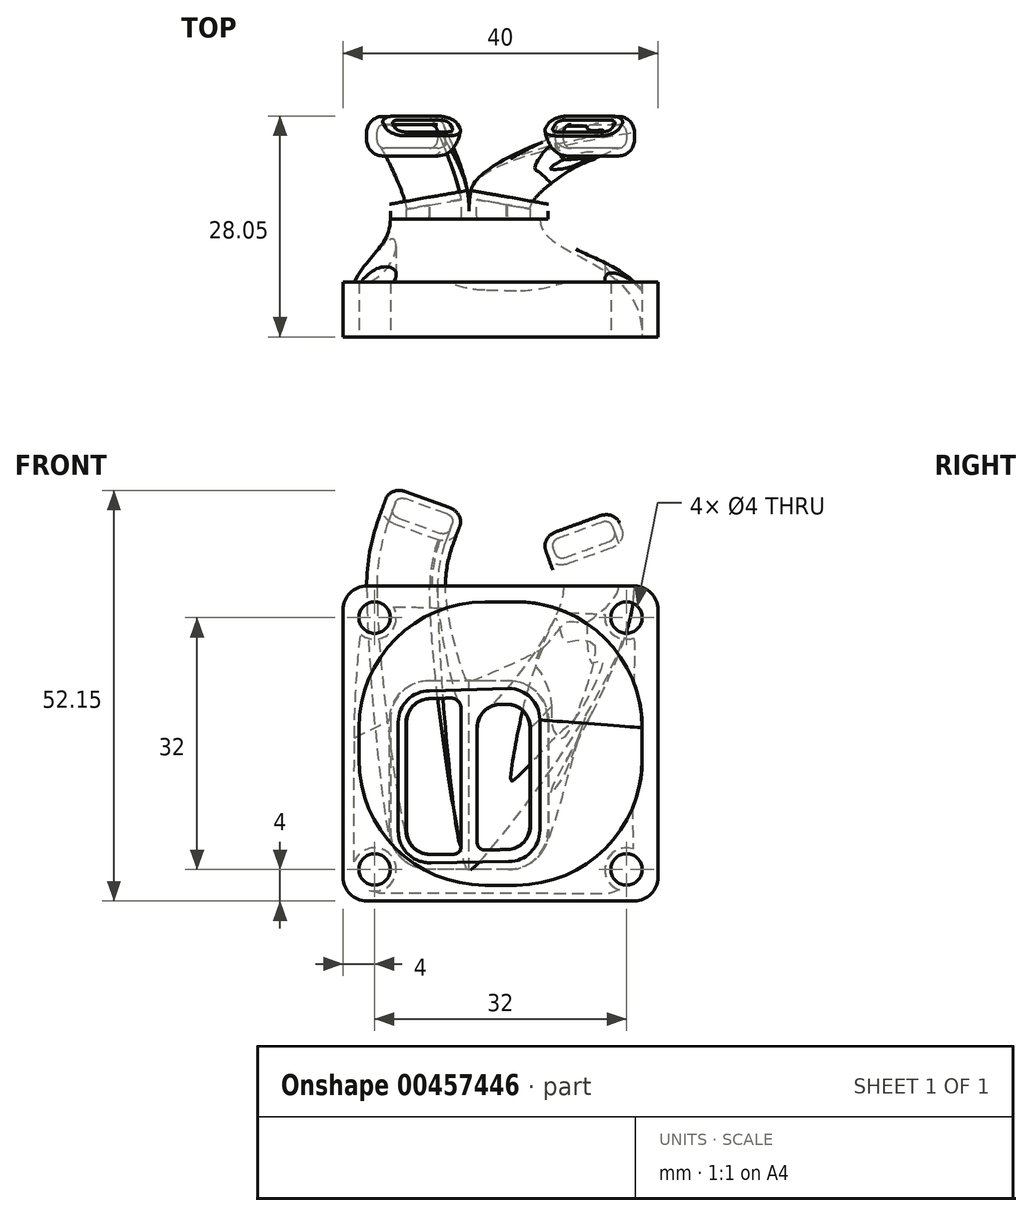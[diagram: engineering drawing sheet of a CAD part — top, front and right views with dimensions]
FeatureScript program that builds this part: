
annotation { "Feature Type Name" : "Feature", "Feature Type Description" : "" }
export const myFeature = defineFeature(function(context is Context, id is Id, definition is map)
    precondition{}
    {
        {
            var Q0;
            Q0=qCreatedBy(makeId("Front.planeOp"),FACE);
            var sketch = newSketch(context, id + "F0", { "sketchPlane" : qUnion([Q0])});
            skLineSegment(sketch, "E0", {"start": v(0, 0) * mm, "end": v(0, 17) * mm});
            skLineSegment(sketch, "E1", {"start": v(3, 20) * mm, "end": v(37, 20) * mm});
            skLineSegment(sketch, "E2", {"start": v(40, 17) * mm, "end": v(40, -17) * mm});
            skLineSegment(sketch, "E3", {"start": v(37, -20) * mm, "end": v(3, -20) * mm});
            skLineSegment(sketch, "E4", {"start": v(0, -17) * mm, "end": v(0, 0) * mm});
            skPoint(sketch, "E5.visualSharp", {"position": v(40, 20) * mm});
            skArc(sketch, "E5.filletArc", {"start": v(40, 17) * mm, "mid": v(39.12, 19.12) * mm, "end": v(37, 20) * mm});
            skPoint(sketch, "E6.visualSharp", {"position": v(40, -20) * mm});
            skArc(sketch, "E6.filletArc", {"start": v(37, -20) * mm, "mid": v(39.12, -19.12) * mm, "end": v(40, -17) * mm});
            skPoint(sketch, "E7.visualSharp", {"position": v(0, -20) * mm});
            skArc(sketch, "E7.filletArc", {"start": v(0, -17) * mm, "mid": v(0.88, -19.12) * mm, "end": v(3, -20) * mm});
            skPoint(sketch, "E8.visualSharp", {"position": v(0, 20) * mm});
            skArc(sketch, "E8.filletArc", {"start": v(3, 20) * mm, "mid": v(0.88, 19.12) * mm, "end": v(0, 17) * mm});
            skSolve(sketch);
        }
        {
            var Q0;
            Q0=qCreatedBy(makeId("Top.planeOp"),FACE);
            cPlane(context, id + "F1", {"entities" : qUnion([Q0]), "cplaneType" : CPlaneType.OFFSET, "offset" : 20 * mm, "width" : 150 * mm, "height" : 150 * mm});
        }
        {
            var Q0;
            Q0=qCreatedBy(id+"F1.planeOp",FACE);
            var sketch = newSketch(context, id + "F2", { "sketchPlane" : qUnion([Q0])});
            skLineSegment(sketch, "E9", {"start": v(3, 26) * mm, "end": v(3, 25) * mm});
            skLineSegment(sketch, "E10", {"start": v(5, 23) * mm, "end": v(11, 23) * mm});
            skLineSegment(sketch, "E11", {"start": v(13, 25) * mm, "end": v(13, 26) * mm});
            skLineSegment(sketch, "E12", {"start": v(37, 26) * mm, "end": v(37, 25) * mm});
            skLineSegment(sketch, "E13", {"start": v(35, 23) * mm, "end": v(29, 23) * mm});
            skLineSegment(sketch, "E14", {"start": v(27, 25) * mm, "end": v(27, 26) * mm});
            skLineSegment(sketch, "E15", {"start": v(5, 28) * mm, "end": v(11, 28) * mm});
            skLineSegment(sketch, "E16", {"start": v(29, 28) * mm, "end": v(35, 28) * mm});
            skPoint(sketch, "E17.visualSharp", {"position": v(13, 28) * mm});
            skArc(sketch, "E17.filletArc", {"start": v(13, 26) * mm, "mid": v(12.41, 27.41) * mm, "end": v(11, 28) * mm});
            skPoint(sketch, "E18.visualSharp", {"position": v(13, 23) * mm});
            skArc(sketch, "E18.filletArc", {"start": v(11, 23) * mm, "mid": v(12.41, 23.59) * mm, "end": v(13, 25) * mm});
            skPoint(sketch, "E19.visualSharp", {"position": v(3, 23) * mm});
            skArc(sketch, "E19.filletArc", {"start": v(3, 25) * mm, "mid": v(3.59, 23.59) * mm, "end": v(5, 23) * mm});
            skPoint(sketch, "E20.visualSharp", {"position": v(3, 28) * mm});
            skArc(sketch, "E20.filletArc", {"start": v(5, 28) * mm, "mid": v(3.59, 27.41) * mm, "end": v(3, 26) * mm});
            skPoint(sketch, "E21.visualSharp", {"position": v(27, 28) * mm});
            skArc(sketch, "E21.filletArc", {"start": v(29, 28) * mm, "mid": v(27.59, 27.41) * mm, "end": v(27, 26) * mm});
            skPoint(sketch, "E22.visualSharp", {"position": v(27, 23) * mm});
            skArc(sketch, "E22.filletArc", {"start": v(27, 25) * mm, "mid": v(27.59, 23.59) * mm, "end": v(29, 23) * mm});
            skPoint(sketch, "E23.visualSharp", {"position": v(37, 23) * mm});
            skArc(sketch, "E23.filletArc", {"start": v(35, 23) * mm, "mid": v(36.41, 23.59) * mm, "end": v(37, 25) * mm});
            skPoint(sketch, "E24.visualSharp", {"position": v(37, 28) * mm});
            skArc(sketch, "E24.filletArc", {"start": v(37, 26) * mm, "mid": v(36.41, 27.41) * mm, "end": v(35, 28) * mm});
            skSolve(sketch);
        }
        {
            var Q0;
            Q0=qCreatedBy(makeId("Front.planeOp"),FACE);
            cPlane(context, id + "F3", {"entities" : qUnion([Q0]), "cplaneType" : CPlaneType.OFFSET, "offset" : 15 * mm, "oppositeDirection" : true, "width" : 150 * mm, "height" : 150 * mm});
        }
        {
            var Q0;
            Q0=qCreatedBy(id+"F3.planeOp",FACE);
            var sketch = newSketch(context, id + "F4", { "sketchPlane" : qUnion([Q0])});
            skLineSegment(sketch, "E25", {"start": v(11, 8) * mm, "end": v(21, 8) * mm});
            skLineSegment(sketch, "E26", {"start": v(26, 3) * mm, "end": v(26, -11) * mm});
            skLineSegment(sketch, "E27", {"start": v(21, -16) * mm, "end": v(11, -16) * mm});
            skLineSegment(sketch, "E28", {"start": v(6, 3) * mm, "end": v(6, -11) * mm});
            skPoint(sketch, "E29.visualSharp", {"position": v(6, 8) * mm});
            skArc(sketch, "E29.filletArc", {"start": v(11, 8) * mm, "mid": v(7.46, 6.54) * mm, "end": v(6, 3) * mm});
            skPoint(sketch, "E30.visualSharp", {"position": v(6, -16) * mm});
            skArc(sketch, "E30.filletArc", {"start": v(6, -11) * mm, "mid": v(7.46, -14.54) * mm, "end": v(11, -16) * mm});
            skPoint(sketch, "E31.visualSharp", {"position": v(26, -16) * mm});
            skArc(sketch, "E31.filletArc", {"start": v(21, -16) * mm, "mid": v(24.54, -14.54) * mm, "end": v(26, -11) * mm});
            skPoint(sketch, "E32.visualSharp", {"position": v(26, 8) * mm});
            skArc(sketch, "E32.filletArc", {"start": v(26, 3) * mm, "mid": v(24.54, 6.54) * mm, "end": v(21, 8) * mm});
            skSolve(sketch);
        }
        {
            var Q0;
            Q0=qSketchRegion(id+"F0",true);
            var Q1;
            Q1=makeQuery(id+"F4.imprint","IMPRINT",FACE,{"disambiguationData":[TD([[makeQuery(id+"F4.imprint","IMPRINT",EDGE,{"derivedFrom":sQuery(id+"F4.wireOp",EDGE,"E25")}),-1.0]])]});
            loft(context, id + "F5", {"startCondition" : LoftEndDerivativeType.NORMAL_TO_PROFILE, "startMagnitude" : 2, "endCondition" : LoftEndDerivativeType.NORMAL_TO_PROFILE, "endMagnitude" : 1, "sheetProfilesArray" : [{ "sheetProfileEntities" : qUnion([Q0]) }, { "sheetProfileEntities" : qUnion([Q1]) }]});
        }
        {
            var Q0;
            Q0=makeQuery(id+"F5.opLoft","CAP_FACE",FACE,{"disambiguationData":[OSD([makeQuery(id+"F4.imprint","IMPRINT",FACE,{"disambiguationData":[TD([[makeQuery(id+"F4.imprint","IMPRINT",EDGE,{"derivedFrom":sQuery(id+"F4.wireOp",EDGE,"E25")}),-1.0]])]})])],"isStart":true});
            extrude(context, id + "F6", {"entities" : qUnion([Q0]), "operationType" : NewBodyOperationType.ADD, "depth" : 1 * mm});
        }
        {
            var Q0;
            Q0=makeQuery(id+"F6.opExtrude","CAP_FACE",FACE,{"disambiguationData":[OSD([makeQuery(id+"F4.imprint","IMPRINT",FACE,{"disambiguationData":[TD([[makeQuery(id+"F4.imprint","IMPRINT",EDGE,{"derivedFrom":sQuery(id+"F4.wireOp",EDGE,"E25")}),-1.0]])]})])],"isStart":false});
            var sketch = newSketch(context, id + "F7", { "sketchPlane" : qUnion([Q0])});
            skLineSegment(sketch, "E33", {"start": v(-16, -16) * mm, "end": v(-16, 8) * mm});
            skLineSegment(sketch, "E34", {"start": v(-16, 8) * mm, "end": v(-16, 5) * mm});
            skLineSegment(sketch, "E35", {"start": v(-16, 8) * mm, "end": v(-17.5, 8) * mm});
            skLineSegment(sketch, "E36", {"start": v(-16, -16) * mm, "end": v(-16, -13) * mm});
            skLineSegment(sketch, "E37", {"start": v(-16, -16) * mm, "end": v(-17.75, -16) * mm});
            skLineSegment(sketch, "E38", {"start": v(-6, -11) * mm, "end": v(-6, 3) * mm});
            skLineSegment(sketch, "E39", {"start": v(-16, -16) * mm, "end": v(-11, -16) * mm});
            skLineSegment(sketch, "E40", {"start": v(-11, 8) * mm, "end": v(-16, 8) * mm});
            skPoint(sketch, "E41.visualSharp", {"position": v(-6, 8) * mm});
            skArc(sketch, "E41.filletArc", {"start": v(-6, 3) * mm, "mid": v(-7.46, 6.54) * mm, "end": v(-11, 8) * mm});
            skPoint(sketch, "E42.visualSharp", {"position": v(-6, -16) * mm});
            skArc(sketch, "E42.filletArc", {"start": v(-11, -16) * mm, "mid": v(-7.46, -14.54) * mm, "end": v(-6, -11) * mm});
            skLineSegment(sketch, "E43", {"start": v(-11, -16) * mm, "end": v(-14.95, -16) * mm});
            skLineSegment(sketch, "E44", {"start": v(-14.95, -16) * mm, "end": v(-16, -16) * mm});
            skLineSegment(sketch, "E45", {"start": v(-11, 8) * mm, "end": v(-14.63, 8) * mm});
            skLineSegment(sketch, "E46", {"start": v(-14.63, 8) * mm, "end": v(-16, 8) * mm});
            skSolve(sketch);
        }
        {
            var Q0;
            Q0=makeQuery(id+"F7.imprint","IMPRINT",FACE,{"disambiguationData":[TD([[makeQuery(id+"F7.imprint","IMPRINT",EDGE,{"derivedFrom":sQuery(id+"F7.wireOp",EDGE,"E33")}),-1.0]])]});
            var sketch = newSketch(context, id + "F8", { "sketchPlane" : qUnion([Q0])});
            skLineSegment(sketch, "E47", {"start": v(-1, -4.8) * mm, "end": v(-1, 5.62) * mm});
            skLineSegment(sketch, "E48", {"start": v(-31, 5.62) * mm, "end": v(-31, -15.15) * mm});
            skSolve(sketch);
        }
        {
            var Q0;
            Q0=makeQuery(id+"F7.imprint","IMPRINT",FACE,{"disambiguationData":[TD([[makeQuery(id+"F7.imprint","IMPRINT",EDGE,{"derivedFrom":sQuery(id+"F7.wireOp",EDGE,"E33")}),1.0]])]});
            var Q1;
            Q1=sQuery(id+"F8.wireOp",EDGE,"E48");
            revolve(context, id + "F9", {"operationType" : NewBodyOperationType.ADD, "entities" : qUnion([Q0]), "axis" : qUnion([Q1]), "revolveType" : RevolveType.ONE_DIRECTION, "angle" : 10 * degree});
        }
        {
            var Q0;
            Q0=makeQuery(id+"F7.imprint","IMPRINT",FACE,{"disambiguationData":[TD([[makeQuery(id+"F7.imprint","IMPRINT",EDGE,{"derivedFrom":sQuery(id+"F7.wireOp",EDGE,"E33")}),-1.0]])]});
            var Q1;
            Q1=sQuery(id+"F8.wireOp",EDGE,"E47");
            revolve(context, id + "F10", {"operationType" : NewBodyOperationType.ADD, "entities" : qUnion([Q0]), "axis" : qUnion([Q1]), "revolveType" : RevolveType.ONE_DIRECTION, "angle" : 10 * degree});
        }
        {
            var Q1;
            Q1=makeQuery(id+"F9.opRevolve","CAP_FACE",FACE,{"disambiguationData":[OSD([sQuery(id+"F4.wireOp",EDGE,"E25"),sQuery(id+"F4.wireOp",EDGE,"E26"),sQuery(id+"F4.wireOp",EDGE,"E27"),sQuery(id+"F4.wireOp",EDGE,"E29.filletArc"),sQuery(id+"F4.wireOp",EDGE,"E30.filletArc"),sQuery(id+"F4.wireOp",EDGE,"E31.filletArc"),sQuery(id+"F4.wireOp",EDGE,"E32.filletArc"),sQuery(id+"F7.wireOp",EDGE,"E33"),sQuery(id+"F7.wireOp",EDGE,"E34"),sQuery(id+"F7.wireOp",EDGE,"E35"),sQuery(id+"F7.wireOp",EDGE,"E36"),sQuery(id+"F7.wireOp",EDGE,"E37")])],"isStart":false});
            var Q2;
            Q2=makeQuery(id+"F2.imprint","IMPRINT",FACE,{"disambiguationData":[TD([[makeQuery(id+"F2.imprint","IMPRINT",EDGE,{"derivedFrom":sQuery(id+"F2.wireOp",EDGE,"E12")}),-1.0]])]});
            loft(context, id + "F11", {"operationType" : NewBodyOperationType.ADD, "startCondition" : LoftEndDerivativeType.NORMAL_TO_PROFILE, "startMagnitude" : 1, "endCondition" : LoftEndDerivativeType.NORMAL_TO_PROFILE, "endMagnitude" : 1, "sheetProfilesArray" : [{ "sheetProfileEntities" : qUnion([Q1]) }, { "sheetProfileEntities" : qUnion([Q2]) }]});
        }
        {
            var Q1;
            Q1=makeQuery(id+"F10.opRevolve","CAP_FACE",FACE,{"disambiguationData":[OSD([sQuery(id+"F0.wireOp",EDGE,"E0"),sQuery(id+"F0.wireOp",EDGE,"E4"),sQuery(id+"F4.wireOp",EDGE,"E25"),sQuery(id+"F4.wireOp",EDGE,"E27"),sQuery(id+"F4.wireOp",EDGE,"E28"),sQuery(id+"F4.wireOp",EDGE,"E29.filletArc"),sQuery(id+"F4.wireOp",EDGE,"E30.filletArc"),sQuery(id+"F4.wireOp",EDGE,"E31.filletArc"),sQuery(id+"F4.wireOp",EDGE,"E32.filletArc"),sQuery(id+"F7.wireOp",EDGE,"E33"),sQuery(id+"F7.wireOp",EDGE,"eooe6Qcx-zl0v-XeAy-R2di-PJaWR5bL0I77"),sQuery(id+"F7.wireOp",EDGE,"E34"),sQuery(id+"F7.wireOp",EDGE,"E36"),sQuery(id+"F7.wireOp",EDGE,"KL9OZESf-6kgJ-Yt0d-4tDR-3qCoX2jgUDdf")])],"isStart":false});
            var Q2;
            Q2=makeQuery(id+"F2.imprint","IMPRINT",FACE,{"disambiguationData":[TD([[makeQuery(id+"F2.imprint","IMPRINT",EDGE,{"derivedFrom":sQuery(id+"F2.wireOp",EDGE,"E9")}),1.0]])]});
            var Q3;
            Q3=makeQuery(id+"F10.opRevolve","CAP_VERTEX",VERTEX,{"disambiguationData":[OSD([sQuery(id+"F7.wireOp",EDGE,"E34"),sQuery(id+"F7.wireOp",EDGE,"E35"),sQuery(id+"F7.wireOp",EDGE,"E46")])],"isStart":false});
            var Q4;
            Q4=sQuery(id+"F2.wireOp",VERTEX,"E11.start");
            loft(context, id + "F12", {"operationType" : NewBodyOperationType.ADD, "startCondition" : LoftEndDerivativeType.NORMAL_TO_PROFILE, "startMagnitude" : 1, "endCondition" : LoftEndDerivativeType.NORMAL_TO_PROFILE, "endMagnitude" : 1, "sheetProfilesArray" : [{ "sheetProfileEntities" : qUnion([Q1]) }, { "sheetProfileEntities" : qUnion([Q2]) }], "matchConnections" : true, "connections" : [{ "connectionEntities" : qUnion([Q3, Q4]), "connectionEdgeQueries" : qUnion([]), "connectionEdgeParameters" : [] }]});
        }
        {
            var Q0;
            Q0=makeQuery(id+"F2.imprint","IMPRINT",FACE,{"disambiguationData":[TD([[makeQuery(id+"F2.imprint","IMPRINT",EDGE,{"derivedFrom":sQuery(id+"F2.wireOp",EDGE,"E9")}),1.0]])]});
            var sketch = newSketch(context, id + "F13", { "sketchPlane" : qUnion([Q0])});
            skLineSegment(sketch, "E49", {"start": v(12, 26) * mm, "end": v(12, 25) * mm});
            skLineSegment(sketch, "E50", {"start": v(11, 24) * mm, "end": v(5.3, 24) * mm});
            skLineSegment(sketch, "E51", {"start": v(4.3, 25) * mm, "end": v(4.3, 26) * mm});
            skLineSegment(sketch, "E52", {"start": v(5.3, 27) * mm, "end": v(11, 27) * mm});
            skPoint(sketch, "E53.visualSharp", {"position": v(4.3, 27) * mm});
            skArc(sketch, "E53.filletArc", {"start": v(5.3, 27) * mm, "mid": v(4.58, 26.7) * mm, "end": v(4.3, 26) * mm});
            skPoint(sketch, "E54.visualSharp", {"position": v(4.3, 24) * mm});
            skArc(sketch, "E54.filletArc", {"start": v(4.3, 25) * mm, "mid": v(4.58, 24.3) * mm, "end": v(5.3, 24) * mm});
            skPoint(sketch, "E55.visualSharp", {"position": v(12, 27) * mm});
            skArc(sketch, "E55.filletArc", {"start": v(12, 26) * mm, "mid": v(11.7, 26.7) * mm, "end": v(11, 27) * mm});
            skPoint(sketch, "E56.visualSharp", {"position": v(12, 24) * mm});
            skArc(sketch, "E56.filletArc", {"start": v(11, 24) * mm, "mid": v(11.7, 24.3) * mm, "end": v(12, 25) * mm});
            skLineSegment(sketch, "E57", {"start": v(36, 26) * mm, "end": v(36, 25) * mm});
            skLineSegment(sketch, "E58", {"start": v(35, 24) * mm, "end": v(29, 24) * mm});
            skLineSegment(sketch, "E59", {"start": v(28, 25) * mm, "end": v(28, 26) * mm});
            skLineSegment(sketch, "E60", {"start": v(29, 27) * mm, "end": v(35, 27) * mm});
            skPoint(sketch, "E61.visualSharp", {"position": v(28, 27) * mm});
            skArc(sketch, "E61.filletArc", {"start": v(29, 27) * mm, "mid": v(28.3, 26.7) * mm, "end": v(28, 26) * mm});
            skPoint(sketch, "E62.visualSharp", {"position": v(28, 24) * mm});
            skArc(sketch, "E62.filletArc", {"start": v(28, 25) * mm, "mid": v(28.3, 24.3) * mm, "end": v(29, 24) * mm});
            skPoint(sketch, "E63.visualSharp", {"position": v(36, 24) * mm});
            skArc(sketch, "E63.filletArc", {"start": v(35, 24) * mm, "mid": v(35.7, 24.3) * mm, "end": v(36, 25) * mm});
            skPoint(sketch, "E64.visualSharp", {"position": v(36, 27) * mm});
            skArc(sketch, "E64.filletArc", {"start": v(36, 26) * mm, "mid": v(35.7, 26.7) * mm, "end": v(35, 27) * mm});
            skSolve(sketch);
        }
        {
            var Q0;
            Q0=makeQuery(id+"F0.imprint","IMPRINT",FACE,{"disambiguationData":[TD([[makeQuery(id+"F0.imprint","IMPRINT",EDGE,{"derivedFrom":sQuery(id+"F0.wireOp",EDGE,"E0")}),-1.0]])]});
            var sketch = newSketch(context, id + "F14", { "sketchPlane" : qUnion([Q0])});
            skLineSegment(sketch, "E65", {"start": v(22, -18) * mm, "end": v(18, -18) * mm});
            skLineSegment(sketch, "E66", {"start": v(2, -2) * mm, "end": v(2, 2) * mm});
            skLineSegment(sketch, "E67", {"start": v(38, -2) * mm, "end": v(38, 2) * mm});
            skLineSegment(sketch, "E68", {"start": v(22, 18) * mm, "end": v(18, 18) * mm});
            skPoint(sketch, "E69.visualSharp", {"position": v(2, -18) * mm});
            skArc(sketch, "E69.filletArc", {"start": v(2, -2) * mm, "mid": v(6.69, -13.31) * mm, "end": v(18, -18) * mm});
            skPoint(sketch, "E70.visualSharp", {"position": v(2, 18) * mm});
            skArc(sketch, "E70.filletArc", {"start": v(18, 18) * mm, "mid": v(6.69, 13.31) * mm, "end": v(2, 2) * mm});
            skPoint(sketch, "E71.visualSharp", {"position": v(38, 18) * mm});
            skArc(sketch, "E71.filletArc", {"start": v(38, 2) * mm, "mid": v(33.31, 13.31) * mm, "end": v(22, 18) * mm});
            skPoint(sketch, "E72.visualSharp", {"position": v(38, -18) * mm});
            skArc(sketch, "E72.filletArc", {"start": v(22, -18) * mm, "mid": v(33.31, -13.31) * mm, "end": v(38, -2) * mm});
            skSolve(sketch);
        }
        {
            var Q0;
            Q0=qCreatedBy(id+"F3.planeOp",FACE);
            var sketch = newSketch(context, id + "F15", { "sketchPlane" : qUnion([Q0])});
            skLineSegment(sketch, "E73", {"start": v(25, 3) * mm, "end": v(25, -11) * mm});
            skLineSegment(sketch, "E74", {"start": v(7, -11.15) * mm, "end": v(7, 2.7) * mm});
            skPoint(sketch, "E75.visualSharp", {"position": v(25, -15) * mm});
            skArc(sketch, "E75.filletArc", {"start": v(21, -15) * mm, "mid": v(23.83, -13.83) * mm, "end": v(25, -11) * mm});
            skPoint(sketch, "E76.visualSharp", {"position": v(25, 7) * mm});
            skArc(sketch, "E76.filletArc", {"start": v(25, 3) * mm, "mid": v(23.83, 5.83) * mm, "end": v(21, 7) * mm});
            skPoint(sketch, "E77.visualSharp", {"position": v(7, 6.7) * mm});
            skArc(sketch, "E77.filletArc", {"start": v(11, 6.7) * mm, "mid": v(8.18, 5.53) * mm, "end": v(7, 2.7) * mm});
            skPoint(sketch, "E78.visualSharp", {"position": v(7, -15.3) * mm});
            skArc(sketch, "E78.filletArc", {"start": v(7, -11.15) * mm, "mid": v(8.23, -14.03) * mm, "end": v(11.16, -15.14) * mm});
            skLineSegment(sketch, "E79", {"start": v(21, -15) * mm, "end": v(11.16, -15.14) * mm});
            skLineSegment(sketch, "E80", {"start": v(11, 6.7) * mm, "end": v(21, 7) * mm});
            skSolve(sketch);
        }
        {
            var Q1;
            Q1=qSketchRegion(id+"F15",true);
            var Q2;
            Q2=qSketchRegion(id+"F14",true);
            loft(context, id + "F16", {"operationType" : NewBodyOperationType.REMOVE, "startCondition" : LoftEndDerivativeType.NORMAL_TO_PROFILE, "startMagnitude" : 1, "endCondition" : LoftEndDerivativeType.NORMAL_TO_PROFILE, "endMagnitude" : 2, "sheetProfilesArray" : [{ "sheetProfileEntities" : qUnion([Q1]) }, { "sheetProfileEntities" : qUnion([Q2]) }]});
        }
        {
            var Q0;
            Q0=qCreatedBy(id+"F3.planeOp",FACE);
            var sketch = newSketch(context, id + "F17", { "sketchPlane" : qUnion([Q0])});
            skLineSegment(sketch, "E81", {"start": v(8, -11.07) * mm, "end": v(8, 2.7) * mm});
            skLineSegment(sketch, "E82", {"start": v(10.92, 5.7) * mm, "end": v(13.66, 5.78) * mm});
            skLineSegment(sketch, "E83", {"start": v(11, -14.07) * mm, "end": v(14, -14.07) * mm});
            skPoint(sketch, "E84.visualSharp", {"position": v(8, 5.6) * mm});
            skArc(sketch, "E84.filletArc", {"start": v(10.92, 5.7) * mm, "mid": v(8.85, 4.79) * mm, "end": v(8, 2.7) * mm});
            skPoint(sketch, "E85.visualSharp", {"position": v(24, 6.24) * mm});
            skPoint(sketch, "E86.visualSharp", {"position": v(24, -14.07) * mm});
            skPoint(sketch, "E87.visualSharp", {"position": v(8, -14.07) * mm});
            skArc(sketch, "E87.filletArc", {"start": v(8, -11.07) * mm, "mid": v(8.88, -13.2) * mm, "end": v(11, -14.07) * mm});
            skLineSegment(sketch, "E88", {"start": v(15, 4.48) * mm, "end": v(15, -13.07) * mm});
            skPoint(sketch, "E89.visualSharp", {"position": v(15, 5.82) * mm});
            skArc(sketch, "E89.filletArc", {"start": v(15, 4.48) * mm, "mid": v(14.6, 5.41) * mm, "end": v(13.66, 5.78) * mm});
            skPoint(sketch, "E90.visualSharp", {"position": v(15, -14.07) * mm});
            skArc(sketch, "E90.filletArc", {"start": v(14, -14.07) * mm, "mid": v(14.71, -13.78) * mm, "end": v(15, -13.07) * mm});
            skSolve(sketch);
        }
        {
            var Q0;
            Q0=qCreatedBy(id+"F3.planeOp",FACE);
            var sketch = newSketch(context, id + "F18", { "sketchPlane" : qUnion([Q0])});
            skLineSegment(sketch, "E91", {"start": v(23.8, 2) * mm, "end": v(23.8, -10.46) * mm});
            skLineSegment(sketch, "E92", {"start": v(20.88, -13.46) * mm, "end": v(18.03, -13.53) * mm});
            skLineSegment(sketch, "E93", {"start": v(17, -12.54) * mm, "end": v(17, 1.97) * mm});
            skLineSegment(sketch, "E94", {"start": v(19.92, 4.97) * mm, "end": v(20.72, 5) * mm});
            skPoint(sketch, "E95.visualSharp", {"position": v(17, -13.56) * mm});
            skArc(sketch, "E95.filletArc", {"start": v(17, -12.54) * mm, "mid": v(17.3, -13.25) * mm, "end": v(18.03, -13.53) * mm});
            skPoint(sketch, "E96.visualSharp", {"position": v(17, 4.9) * mm});
            skArc(sketch, "E96.filletArc", {"start": v(19.92, 4.97) * mm, "mid": v(17.85, 4.06) * mm, "end": v(17, 1.97) * mm});
            skPoint(sketch, "E97.visualSharp", {"position": v(23.8, 5.08) * mm});
            skArc(sketch, "E97.filletArc", {"start": v(23.8, 2) * mm, "mid": v(22.9, 4.14) * mm, "end": v(20.72, 5) * mm});
            skPoint(sketch, "E98.visualSharp", {"position": v(23.8, -13.38) * mm});
            skArc(sketch, "E98.filletArc", {"start": v(20.88, -13.46) * mm, "mid": v(22.95, -12.55) * mm, "end": v(23.8, -10.46) * mm});
            skSolve(sketch);
        }
        {
            var Q0;
            Q0=qSketchRegion(id+"F17",true);
            var Q1;
            Q1=sQuery(id+"F8.wireOp",EDGE,"E47");
            revolve(context, id + "F19", {"operationType" : NewBodyOperationType.REMOVE, "entities" : qUnion([Q0]), "axis" : qUnion([Q1]), "revolveType" : RevolveType.ONE_DIRECTION, "angle" : 10 * degree});
        }
        {
            var Q0;
            Q0=qSketchRegion(id+"F18",true);
            var Q1;
            Q1=sQuery(id+"F8.wireOp",EDGE,"E48");
            revolve(context, id + "F20", {"operationType" : NewBodyOperationType.REMOVE, "entities" : qUnion([Q0]), "axis" : qUnion([Q1]), "revolveType" : RevolveType.ONE_DIRECTION, "angle" : 10 * degree});
        }
        {
            var Q1;
            Q1=makeQuery(id+"F20.boolean.opBoolean","COPY",FACE,{"derivedFrom":makeQuery(id+"F20.opRevolve","CAP_FACE",FACE,{"disambiguationData":[OSD([sQuery(id+"F18.wireOp",EDGE,"E91"),sQuery(id+"F18.wireOp",EDGE,"E92"),sQuery(id+"F18.wireOp",EDGE,"E93"),sQuery(id+"F18.wireOp",EDGE,"E94"),sQuery(id+"F18.wireOp",EDGE,"E95.filletArc"),sQuery(id+"F18.wireOp",EDGE,"E96.filletArc"),sQuery(id+"F18.wireOp",EDGE,"E97.filletArc"),sQuery(id+"F18.wireOp",EDGE,"E98.filletArc")])],"isStart":false})});
            var Q2;
            Q2=makeQuery(id+"F13.imprint","IMPRINT",FACE,{"disambiguationData":[TD([[makeQuery(id+"F13.imprint","IMPRINT",EDGE,{"derivedFrom":sQuery(id+"F13.wireOp",EDGE,"E57")}),-1.0]])]});
            loft(context, id + "F21", {"operationType" : NewBodyOperationType.REMOVE, "startCondition" : LoftEndDerivativeType.NORMAL_TO_PROFILE, "startMagnitude" : 1, "endCondition" : LoftEndDerivativeType.NORMAL_TO_PROFILE, "endMagnitude" : 1, "sheetProfilesArray" : [{ "sheetProfileEntities" : qUnion([Q1]) }, { "sheetProfileEntities" : qUnion([Q2]) }]});
        }
        {
            var Q1;
            Q1=makeQuery(id+"F13.imprint","IMPRINT",FACE,{"disambiguationData":[TD([[makeQuery(id+"F13.imprint","IMPRINT",EDGE,{"derivedFrom":sQuery(id+"F13.wireOp",EDGE,"E49")}),-1.0]])]});
            var Q2;
            Q2=makeQuery(id+"F19.boolean.opBoolean","COPY",FACE,{"derivedFrom":makeQuery(id+"F19.opRevolve","CAP_FACE",FACE,{"disambiguationData":[OSD([sQuery(id+"F17.wireOp",EDGE,"E81"),sQuery(id+"F17.wireOp",EDGE,"E82"),sQuery(id+"F17.wireOp",EDGE,"E83"),sQuery(id+"F17.wireOp",EDGE,"E84.filletArc"),sQuery(id+"F17.wireOp",EDGE,"E87.filletArc"),sQuery(id+"F17.wireOp",EDGE,"E88"),sQuery(id+"F17.wireOp",EDGE,"E89.filletArc"),sQuery(id+"F17.wireOp",EDGE,"E90.filletArc")])],"isStart":false})});
            loft(context, id + "F22", {"operationType" : NewBodyOperationType.REMOVE, "startCondition" : LoftEndDerivativeType.NORMAL_TO_PROFILE, "startMagnitude" : 1, "endCondition" : LoftEndDerivativeType.NORMAL_TO_PROFILE, "endMagnitude" : 1, "sheetProfilesArray" : [{ "sheetProfileEntities" : qUnion([Q1]) }, { "sheetProfileEntities" : qUnion([Q2]) }]});
        }
        {
            var Q0;
            Q0=makeQuery(id+"F13.imprint","IMPRINT",FACE,{"disambiguationData":[TD([[makeQuery(id+"F13.imprint","IMPRINT",EDGE,{"derivedFrom":sQuery(id+"F13.wireOp",EDGE,"E49")}),1.0]])]});
            var sketch = newSketch(context, id + "F23", { "sketchPlane" : qUnion([Q0])});
            skLineSegment(sketch, "E99", {"start": v(11, 27.98) * mm, "end": v(29, 27.98) * mm});
            skLineSegment(sketch, "E100", {"start": v(11, 27.98) * mm, "end": v(11, 32.98) * mm});
            skLineSegment(sketch, "E101", {"start": v(29, 27.98) * mm, "end": v(29, 32.98) * mm});
            skLineSegment(sketch, "E102", {"start": v(29, 32.98) * mm, "end": v(20, 27.98) * mm});
            skLineSegment(sketch, "E103", {"start": v(20, 27.98) * mm, "end": v(11, 32.98) * mm});
            skLineSegment(sketch, "E104", {"start": v(21, 27.98) * mm, "end": v(21, 22.98) * mm});
            skSolve(sketch);
        }
        {
            var Q0;
            Q0=makeQuery(id+"F5.opLoft","CAP_FACE",FACE,{"disambiguationData":[OSD([makeQuery(id+"F0.imprint","IMPRINT",FACE,{"disambiguationData":[TD([[makeQuery(id+"F0.imprint","IMPRINT",EDGE,{"derivedFrom":sQuery(id+"F0.wireOp",EDGE,"E0")}),-1.0]])]})])],"isStart":true});
            var sketch = newSketch(context, id + "F24", { "sketchPlane" : qUnion([Q0])});
            skCircle(sketch, "E105", {"center": v(4, 16) * mm, "radius": 2 * mm});
            skCircle(sketch, "E106", {"center": v(36, 16) * mm, "radius": 2 * mm});
            skCircle(sketch, "E107", {"center": v(36, -16) * mm, "radius": 2 * mm});
            skCircle(sketch, "E108", {"center": v(4, -16) * mm, "radius": 2 * mm});
            skSolve(sketch);
        }
        {
            var Q0;
            Q0=makeQuery(id+"F24.imprint","IMPRINT",FACE,{"disambiguationData":[TD([[makeQuery(id+"F24.imprint","IMPRINT",EDGE,{"derivedFrom":sQuery(id+"F24.wireOp",EDGE,"E105")}),-1.0]])]});
            extrude(context, id + "F25", {"entities" : qUnion([Q0]), "operationType" : NewBodyOperationType.ADD, "oppositeDirection" : true, "depth" : 7 * mm});
        }
        {
            var Q0;
            Q0=makeQuery(id+"F24.imprint","IMPRINT",FACE,{"disambiguationData":[TD([[makeQuery(id+"F24.imprint","IMPRINT",EDGE,{"derivedFrom":sQuery(id+"F24.wireOp",EDGE,"E105")}),1.0]])]});
            var Q1;
            Q1=makeQuery(id+"F24.imprint","IMPRINT",FACE,{"disambiguationData":[TD([[makeQuery(id+"F24.imprint","IMPRINT",EDGE,{"derivedFrom":sQuery(id+"F24.wireOp",EDGE,"E106")}),1.0]])]});
            var Q2;
            Q2=makeQuery(id+"F24.imprint","IMPRINT",FACE,{"disambiguationData":[TD([[makeQuery(id+"F24.imprint","IMPRINT",EDGE,{"derivedFrom":sQuery(id+"F24.wireOp",EDGE,"E107")}),1.0]])]});
            var Q3;
            Q3=makeQuery(id+"F24.imprint","IMPRINT",FACE,{"disambiguationData":[TD([[makeQuery(id+"F24.imprint","IMPRINT",EDGE,{"derivedFrom":sQuery(id+"F24.wireOp",EDGE,"E108")}),1.0]])]});
            var Q4;
            Q4=sQuery(id+"F24.wireOp",EDGE,"E105");
            var Q5;
            Q5=sQuery(id+"F24.wireOp",EDGE,"E106");
            var Q6;
            Q6=sQuery(id+"F24.wireOp",EDGE,"E107");
            var Q7;
            Q7=sQuery(id+"F24.wireOp",EDGE,"E108");
            extrude(context, id + "F26", {"entities" : qUnion([Q0, Q1, Q2, Q3]), "operationType" : NewBodyOperationType.REMOVE, "surfaceEntities" : qUnion([Q4, Q5, Q6, Q7]), "oppositeDirection" : true, "depth" : 15 * mm});
        }
        {
            var Q0;
            Q0=makeQuery(id+"F25.opExtrude","CAP_FACE",FACE,{"disambiguationData":[OSD([sQuery(id+"F0.wireOp",EDGE,"E0"),sQuery(id+"F0.wireOp",EDGE,"E1"),sQuery(id+"F0.wireOp",EDGE,"E2"),sQuery(id+"F0.wireOp",EDGE,"E3"),sQuery(id+"F0.wireOp",EDGE,"E4"),sQuery(id+"F0.wireOp",EDGE,"E5.filletArc"),sQuery(id+"F0.wireOp",EDGE,"E6.filletArc"),sQuery(id+"F0.wireOp",EDGE,"E7.filletArc"),sQuery(id+"F0.wireOp",EDGE,"E8.filletArc"),sQuery(id+"F14.wireOp",EDGE,"E65"),sQuery(id+"F14.wireOp",EDGE,"E66"),sQuery(id+"F14.wireOp",EDGE,"E67"),sQuery(id+"F14.wireOp",EDGE,"E68"),sQuery(id+"F14.wireOp",EDGE,"E69.filletArc"),sQuery(id+"F14.wireOp",EDGE,"E70.filletArc"),sQuery(id+"F14.wireOp",EDGE,"E71.filletArc"),sQuery(id+"F14.wireOp",EDGE,"E72.filletArc"),sQuery(id+"F24.wireOp",EDGE,"E105"),sQuery(id+"F24.wireOp",EDGE,"E106"),sQuery(id+"F24.wireOp",EDGE,"E107"),sQuery(id+"F24.wireOp",EDGE,"E108")])],"isStart":false});
            var sketch = newSketch(context, id + "F27", { "sketchPlane" : qUnion([Q0])});
            skCircle(sketch, "E109", {"center": v(-36, -16) * mm, "radius": 2.75 * mm});
            skLineSegment(sketch, "E110", {"start": v(-36, -16) * mm, "end": v(-4, -16) * mm});
            skCircle(sketch, "E111", {"center": v(-36, 16) * mm, "radius": 2.75 * mm});
            skCircle(sketch, "E112", {"center": v(-4, 16) * mm, "radius": 2.75 * mm});
            skCircle(sketch, "E113", {"center": v(-4, -16) * mm, "radius": 2.75 * mm});
            skSolve(sketch);
        }
        {
            var Q0;
            {var subQ1=sQuery(id+"F24.wireOp",EDGE,"E105");var subQ11=makeQuery(id+"F25.opExtrude","CAP_EDGE",EDGE,{"disambiguationData":[OSD([subQ1])],"isStart":false});Q0=makeQuery(id+"F27.imprint","IMPRINT",FACE,{"disambiguationData":[TD([[makeQuery(id+"F27.imprint","IMPRINT",EDGE,{"derivedFrom":subQ11}),-1.0]])]});}
            var Q1;
            {var subQ0=sQuery(id+"F27.wireOp",EDGE,"E113");var subQ1=makeQuery(id+"F27.imprint","INTERSECT",VERTEX,{"derivedFrom":[sQuery(id+"F27.wireOp",EDGE,"E110"),subQ0]});Q1=makeQuery(id+"F27.imprint","IMPRINT",FACE,{"disambiguationData":[TD([[makeQuery(id+"F27.imprint","IMPRINT",EDGE,{"disambiguationData":[TD([[subQ1,1.0]])],"derivedFrom":subQ0}),1.0]])]});}
            var Q2;
            {var subQ0=sQuery(id+"F24.wireOp",EDGE,"E107");var subQ7=makeQuery(id+"F25.opExtrude","CAP_EDGE",EDGE,{"disambiguationData":[OSD([subQ0])],"isStart":false});Q2=makeQuery(id+"F27.imprint","IMPRINT",FACE,{"disambiguationData":[TD([[makeQuery(id+"F27.imprint","IMPRINT",EDGE,{"derivedFrom":subQ7}),-1.0]])]});}
            var Q3;
            {var subQ1=sQuery(id+"F24.wireOp",EDGE,"E106");var subQ11=makeQuery(id+"F25.opExtrude","CAP_EDGE",EDGE,{"disambiguationData":[OSD([subQ1])],"isStart":false});Q3=makeQuery(id+"F27.imprint","IMPRINT",FACE,{"disambiguationData":[TD([[makeQuery(id+"F27.imprint","IMPRINT",EDGE,{"derivedFrom":subQ11}),-1.0]])]});}
            extrude(context, id + "F28", {"entities" : qUnion([Q0, Q1, Q2, Q3]), "operationType" : NewBodyOperationType.REMOVE, "depth" : 6 * mm});
        }
        {
            var Q0;
            Q0=makeQuery(id+"F23.imprint","IMPRINT",FACE,{"disambiguationData":[TD([[makeQuery(id+"F23.imprint","IMPRINT",EDGE,{"derivedFrom":makeQuery(id+"F13.imprint","IMPRINT",EDGE,{"derivedFrom":sQuery(id+"F13.wireOp",EDGE,"E49")})}),1.0]])]});
            var Q1;
            Q1=sQuery(id+"F13.wireOp",EDGE,"E59");
            revolve(context, id + "F29", {"operationType" : NewBodyOperationType.ADD, "entities" : qUnion([Q0]), "axis" : qUnion([Q1]), "revolveType" : RevolveType.ONE_DIRECTION, "angle" : 20 * degree});
        }
        {
            var Q0;
            Q0=makeQuery(id+"F11.opLoft","CAP_FACE",FACE,{"disambiguationData":[OSD([makeQuery(id+"F2.imprint","IMPRINT",FACE,{"disambiguationData":[TD([[makeQuery(id+"F2.imprint","IMPRINT",EDGE,{"derivedFrom":sQuery(id+"F2.wireOp",EDGE,"E12")}),-1.0]])]})])],"isStart":true});
            var Q1;
            Q1=sQuery(id+"F23.wireOp",EDGE,"E104");
            revolve(context, id + "F30", {"operationType" : NewBodyOperationType.ADD, "entities" : qUnion([Q0]), "axis" : qUnion([Q1]), "revolveType" : RevolveType.ONE_DIRECTION, "angle" : 20 * degree});
        }
        {
            var Q0;
            Q0=makeQuery(id+"F29.opRevolve","CAP_FACE",FACE,{"disambiguationData":[OSD([sQuery(id+"F2.wireOp",EDGE,"E9"),sQuery(id+"F2.wireOp",EDGE,"E10"),sQuery(id+"F2.wireOp",EDGE,"E11"),sQuery(id+"F2.wireOp",EDGE,"E15"),sQuery(id+"F2.wireOp",EDGE,"E17.filletArc"),sQuery(id+"F2.wireOp",EDGE,"E18.filletArc"),sQuery(id+"F2.wireOp",EDGE,"E19.filletArc"),sQuery(id+"F2.wireOp",EDGE,"E20.filletArc"),sQuery(id+"F13.wireOp",EDGE,"E49"),sQuery(id+"F13.wireOp",EDGE,"E50"),sQuery(id+"F13.wireOp",EDGE,"E51"),sQuery(id+"F13.wireOp",EDGE,"E52"),sQuery(id+"F13.wireOp",EDGE,"E53.filletArc"),sQuery(id+"F13.wireOp",EDGE,"E54.filletArc"),sQuery(id+"F13.wireOp",EDGE,"E55.filletArc"),sQuery(id+"F13.wireOp",EDGE,"E56.filletArc"),sQuery(id+"F23.wireOp",EDGE,"E99"),sQuery(id+"F23.wireOp",EDGE,"E100")])],"isStart":false});
            var sketch = newSketch(context, id + "F31", { "sketchPlane" : qUnion([Q0])});
            skLineSegment(sketch, "E114", {"start": v(-1.63, 28.1) * mm, "end": v(0.6, 28.1) * mm});
            skSolve(sketch);
        }
        {
            var Q0;
            Q0=makeQuery(id+"F30.opRevolve","CAP_FACE",FACE,{"disambiguationData":[OSD([makeQuery(id+"F2.imprint","IMPRINT",FACE,{"disambiguationData":[TD([[makeQuery(id+"F2.imprint","IMPRINT",EDGE,{"derivedFrom":sQuery(id+"F2.wireOp",EDGE,"E12")}),-1.0]])]})])],"isStart":false});
            var sketch = newSketch(context, id + "F32", { "sketchPlane" : qUnion([Q0])});
            skLineSegment(sketch, "E115", {"start": v(37.2, 28.12) * mm, "end": v(39.09, 28.12) * mm});
            skSolve(sketch);
        }
        {
            var Q0;
            {var subQ4=sQuery(id+"F23.wireOp",EDGE,"E99");Q0=makeQuery(id+"F31.imprint","IMPRINT",FACE,{"disambiguationData":[TD([[makeQuery(id+"F31.imprint","IMPRINT",EDGE,{"derivedFrom":makeQuery(id+"F29.opRevolve","CAP_EDGE",EDGE,{"disambiguationData":[OSD([subQ4])],"isStart":false})}),-1.0]])]});}
            var Q1;
            Q1=sQuery(id+"F31.wireOp",EDGE,"E114");
            revolve(context, id + "F33", {"operationType" : NewBodyOperationType.ADD, "entities" : qUnion([Q0]), "axis" : qUnion([Q1]), "revolveType" : RevolveType.ONE_DIRECTION, "oppositeDirection" : true, "angle" : 60 * degree});
        }
        {
            var Q0;
            {var subQ3=sQuery(id+"F2.wireOp",EDGE,"E24.filletArc");var subQ10=sQuery(id+"F2.wireOp",EDGE,"E23.filletArc");var subQ14=sQuery(id+"F2.wireOp",EDGE,"E12");Q0=makeQuery(id+"F32.imprint","IMPRINT",FACE,{"disambiguationData":[TD([[makeQuery(id+"F32.imprint","IMPRINT",EDGE,{"derivedFrom":makeQuery(id+"F30.opRevolve","CAP_EDGE",EDGE,{"disambiguationData":[OSD([subQ14,subQ10,subQ3])],"isStart":false})}),1.0]])]});}
            var Q1;
            Q1=sQuery(id+"F32.wireOp",EDGE,"E115");
            revolve(context, id + "F34", {"operationType" : NewBodyOperationType.ADD, "entities" : qUnion([Q0]), "axis" : qUnion([Q1]), "revolveType" : RevolveType.ONE_DIRECTION, "oppositeDirection" : true, "angle" : 60 * degree});
        }
    });
